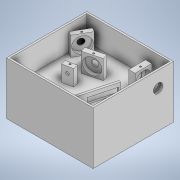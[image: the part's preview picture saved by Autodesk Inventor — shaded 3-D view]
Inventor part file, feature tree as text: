
AUTODESK INVENTOR PART (.ipt)
format: ipt  version: 2022 (Build 260153000, 153)  size: 425,472 bytes
history: native  units: mm
features: extrude x24, sketch x20, thread x4
ambient origin geometry x8: Origin, YZ Plane, XZ Plane, XY Plane, X Axis, Y Axis, Z Axis, Center Point
bodies: Body1 (feature_tree)
feature tree (48):
  sketch  "草图1"  dims[d0=130.0mm d1=140.0mm]
  extrude  "拉伸2"  Depth=140.0mm
  extrude  "拉伸3"  Depth=12.5mm
  extrude  "拉伸4"  Depth=12.5mm
  extrude  "拉伸5"  Depth=25.0mm
  extrude  "拉伸6"  Depth=7.86mm
  extrude  "拉伸7"  Depth=6.0mm
  extrude  "拉伸8"  Depth=29.1mm
  extrude  "拉伸9"  Depth=1.0mm
  extrude  "拉伸10"  Depth=1.5mm
  extrude  "拉伸11"  TaperAngle=0.0deg  [1 undecoded]
  extrude  "拉伸12"  Depth=1.0mm
  extrude  "拉伸13"  TaperAngle=0.0deg  [1 undecoded]
  thread  "螺纹1"  [1 undecoded]
  extrude  "拉伸15"  Depth=2.0mm
  thread  "螺纹3"  [1 undecoded]
  extrude  "拉伸16"  Depth=94.5mm
  extrude  "拉伸17"  Depth=65.945521mm
  thread  "螺纹4"  [1 undecoded]
  extrude  "拉伸18"  Depth=2.5mm
  extrude  "拉伸19"  Depth=5.5mm
  extrude  "拉伸22"  Depth=84.0mm
  thread  "螺纹5"  [1 undecoded]
  sketch  "草图28"  dims[d69=2.5mm d70=63.0mm]
  extrude  "拉伸23"  Depth=25.0mm
  extrude  "拉伸24"  Depth=0.5mm
  extrude  "拉伸25"  Depth=0.5mm
  extrude  "拉伸26"  Depth=0.5mm
  extrude  "拉伸27"  TaperAngle=0.0deg  [1 undecoded]
  extrude  "拉伸28"  Depth=2.0mm
  sketch  "草图3"  dims[d2=25.0mm d3=12.5mm]
  sketch  "草图4"  dims[d4=25.0mm d5=12.5mm]
  sketch  "草图5"  dims[d7=0.52mm d8=25.0mm]
  sketch  "草图6"  dims[d9=6.0mm d11=7.86mm]
  sketch  "草图7"  dims[d13=12.7mm d14=6.0mm]
  sketch  "草图8"  dims[d30=14.55mm d31=29.1mm]
  sketch  "草图10"  dims[d32=1.0mm d33=1.0mm]
  sketch  "草图11"  dims[d34=1.0mm d35=1.5mm]
  sketch  "草图13"  dims[d36=120.0deg d37=0.0mm]
  sketch  "草图16"  dims[d38=1.0mm d39=1.0mm]
  sketch  "草图18"  dims[d40=1.0mm d45=0.0mm d46=2.0mm]
  sketch  "草图19"  dims[d47=2.0mm d48=2.0mm d49=70.5mm]
  sketch  "草图20"  dims[d50=96.518566mm d51=94.5mm]
  sketch  "草图23"  dims[d52=34.0mm d53=65.945521mm d68=20.8mm]
  sketch  "草图30"  dims[d71=5.5mm d72=63.0mm]
  sketch  "草图32"  dims[d73=3.5mm d74=84.0mm d75=47.0mm]
  sketch  "草图33"  dims[d76=12.5mm d77=25.0mm]
  sketch  "草图34"  dims[d78=0.52mm d79=6.0mm d84=14.5mm d85=14.5mm d86=0.0mm d87=2.0mm d88=31.0mm d89=0.0mm d90=26.0mm d91=0.0mm d92=5.0mm d93=0.0mm d94=25.8mm d95=15.0mm d96=13.5mm d100=9.86mm d101=0.0mm d102=15.0mm d103=1.0mm d104=0.0mm d105=1.9mm d106=1.9mm d107=13.1mm d108=8.4mm d109=6.2mm d110=0.0mm d111=25.8mm d112=13.95mm d113=27.9mm d114=15.0mm d115=6.56mm d116=0.0mm d117=25.8mm d118=15.0mm d119=14.5mm d120=6.54mm d121=0.0mm d122=41.8mm d123=9.58mm d124=2.5mm d125=10.21mm d126=2.0mm d127=0.0mm d128=3.0mm d129=3.0mm d130=3.0mm d131=3.0mm d132=40.0mm d133=0.0mm d134=3.0mm d135=3.0mm d136=40.0mm d137=0.0mm d138=3.0mm d139=2.5mm d140=0.0mm d141=2.389mm d142=0.0mm d146=3.0mm d147=2.5mm d148=0.0mm d151=0.389mm d152=0.0mm d153=5.0mm d154=0.0mm d156=2.5mm d157=0.0mm d158=1.55mm d159=0.0mm d160=5.0mm d161=0.0mm d162=0.0mm d163=20.0mm d165=0.0mm d166=8.0mm d167=30.0mm d168=0.0mm d179=8.0mm d180=3.0mm d181=2.5mm d182=0.0mm d183=0.389mm d184=0.0mm d188=15.2mm d192=10.75mm d193=0.0mm d194=4.0mm d195=0.0mm d196=26.0mm d197=0.0mm d198=10.0mm d199=10.0mm d200=0.0mm d201=10.0mm d202=10.0mm d203=0.0mm d204=5.0mm d205=10.0mm d206=0.0mm d207=25.0mm d208=25.0mm d43=0.5mm d44=0.872665mm d155=0.5mm]
note: 7 required parameter values undecoded (feature->parameter linkage not recoverable at this tier; creation-order binding heuristic only, values carry confidence <= 0.55)
